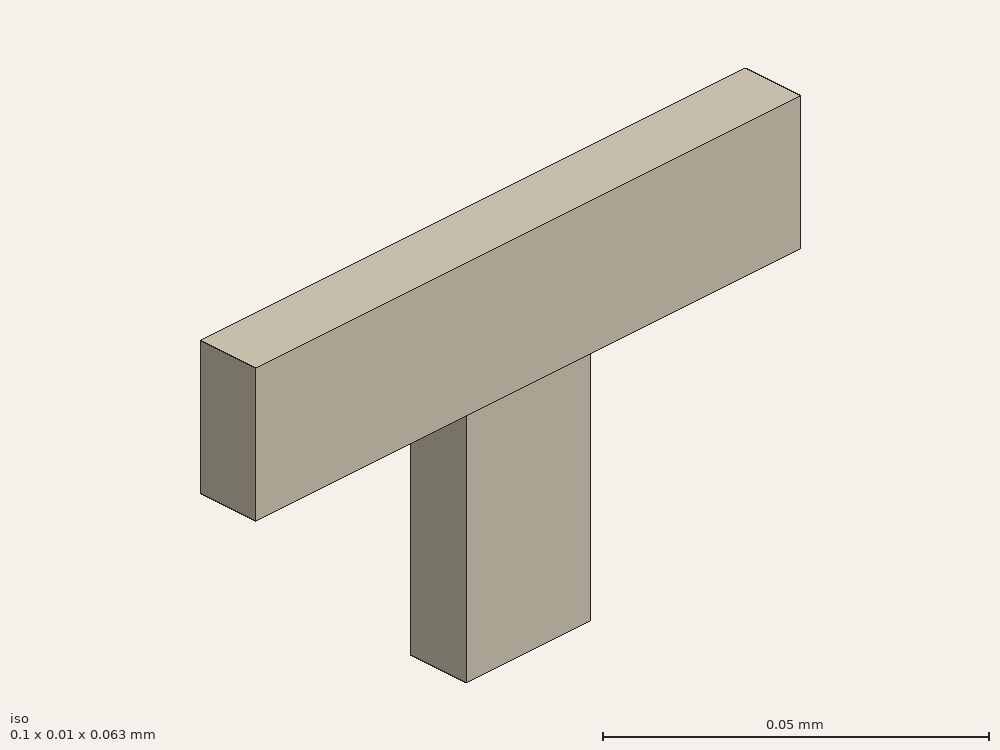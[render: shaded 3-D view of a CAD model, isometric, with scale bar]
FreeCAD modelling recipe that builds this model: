
FCSTD DOCUMENT  (FreeCAD 0.21R33694 (Git))
Label: tee
License: All rights reserved
LicenseURL: http://en.wikipedia.org/wiki/All_rights_reserved
objects: Part::Part2DObjectPython×8, App::FeaturePython×6, Part::Extrusion×2, Part::FeaturePython×2
note: 12 computed .brp shape members not serialized (recipe doc carries the construction recipe); baked Part::Feature solids carry a one-line shape summary decoded from their .brp

FEATURE [Part::Part2DObjectPython] Rectangle  # Draft 2D object (typed FeaturePython)
  Area = 232.258
  ChamferSize = 0
  Columns = 1
  FilletRadius = 0
  Height = 10.16
  Length = 22.86
  MakeFace = true
  Placement = pos=(-11.43,-5.08,0) rot=(0,0,1;0rad)
  Rows = 1
FEATURE [Part::Extrusion] Extrude
  Base = -> Rectangle
  Dir = (0,0,1)
  DirMode = 2
  FaceMakerClass = Part::FaceMakerBullseye
  LengthFwd = 40
  LengthRev = 0
  Solid = false
  Symmetric = false
FEATURE [Part::Part2DObjectPython] Rectangle001  label="_Pport1"  # Draft 2D object (typed FeaturePython)
  Area = 0.000232258
  ChamferSize = 0
  Columns = 1
  FilletRadius = 0
  Height = 0.01016
  Length = 0.02286
  MakeFace = true
  Placement = pos=(-0.01143,-0.00508,0) rot=(0,0,1;0rad)
  Rows = 1
FEATURE [Part::Part2DObjectPython] Line  label="_Pv1"  # Draft 2D object (typed FeaturePython)
  Area = 0
  ChamferSize = 0
  Closed = false
  End = (-1.8e-15,0.00508,0)
  FilletRadius = 0
  Length = 0.01016
  MakeFace = true
  Placement = pos=(0,-0.00508,0) rot=(0,0,1;0rad)
  Points = (2) [(0,0,0),(-1.77605e-15,0.01016,0)]
  Start = (0,-0.00508,0)
  Subdivisions = 0
FEATURE [App::FeaturePython] Text  label="_S1(PV){port1}"  # WARN: FeaturePython — macro-defined, semantics opaque (R4)
  Placement = pos=(0.0413747,-0.017509,0) rot=(0,0,1;0rad)
  Text = .
FEATURE [App::FeaturePython] Text001  label="_S2(PV){port2}"  # WARN: FeaturePython — macro-defined, semantics opaque (R4)
  Placement = pos=(0.0413747,-0.017509,0) rot=(0,0,1;0rad)
  Text = .
FEATURE [App::FeaturePython] Text002  label="_L1(1,voltage){v1}"  # WARN: FeaturePython — macro-defined, semantics opaque (R4)
  Placement = pos=(0.0413747,-0.017509,0) rot=(0,0,1;0rad)
  Text = .
FEATURE [App::FeaturePython] Text003  label="_L2(2,voltage){v2}"  # WARN: FeaturePython — macro-defined, semantics opaque (R4)
  Placement = pos=(0.0413747,-0.017509,0) rot=(0,0,1;0rad)
  Text = .
FEATURE [Part::Part2DObjectPython] Rectangle003  # Draft 2D object (typed FeaturePython)
  Area = 232.258
  ChamferSize = 0
  Columns = 1
  FilletRadius = 0
  Height = 10.16
  Length = 22.86
  MakeFace = true
  Placement = pos=(-11.43,-5.08,100) rot=(0,0,1;0rad)
  Rows = 1
FEATURE [Part::Extrusion] Extrude001
  Base = -> Rectangle003
  Dir = (0,0,1)
  DirMode = 2
  FaceMakerClass = Part::FaceMakerBullseye
  LengthFwd = 100
  LengthRev = 0
  Placement = pos=(150,0,51.43) rot=(0,-1,0;1.5708rad)
  Solid = false
  Symmetric = false
FEATURE [Part::FeaturePython] BooleanFragments  # WARN: FeaturePython — macro-defined, semantics opaque (R4)
  Mode = 0
  Objects = -> [Extrude,Extrude001]
  Tolerance = 0
FEATURE [Part::FeaturePython] Clone  label="scaled"  # Draft clone (typed FeaturePython)
  AttacherType = Attacher::AttachEngine3D
  Fuse = false
  Objects = -> [BooleanFragments]
  Scale = (0.001,0.001,0.001)
FEATURE [Part::Part2DObjectPython] Rectangle004  label="_Pport2"  # Draft 2D object (typed FeaturePython)
  Area = 0.000232258
  ChamferSize = 0
  Columns = 1
  FilletRadius = 0
  Height = 0.02286
  Length = 0.01016
  MakeFace = true
  Placement = pos=(0.05,-0.00508,0.04) rot=(0.57735,0.57735,0.57735;2.0944rad)
  Rows = 1
FEATURE [Part::Part2DObjectPython] Line002  label="_Pv2"  # Draft 2D object (typed FeaturePython)
  Area = 0
  ChamferSize = 0
  Closed = false
  End = (0.05,0.00508,0.05143)
  FilletRadius = 0
  Length = 0.01016
  MakeFace = true
  Placement = pos=(0.05,-0.00508,0.05143) rot=(0.57735,0.57735,0.57735;2.0944rad)
  Points = (2) [(0,0,0),(0.01016,7.10543e-15,0)]
  Start = (0.05,-0.00508,0.05143)
  Subdivisions = 0
FEATURE [Part::Part2DObjectPython] Rectangle005  label="_Pport3"  # Draft 2D object (typed FeaturePython)
  Area = 0.000232258
  ChamferSize = 0
  Columns = 1
  FilletRadius = 0
  Height = 0.02286
  Length = 0.01016
  MakeFace = true
  Placement = pos=(-0.05,0.00508,0.04) rot=(0.57735,-0.57735,-0.57735;2.0944rad)
  Rows = 1
FEATURE [Part::Part2DObjectPython] Line003  label="_Pv3"  # Draft 2D object (typed FeaturePython)
  Area = 0
  ChamferSize = 0
  Closed = false
  End = (-0.05,0.00508,0.05143)
  FilletRadius = 0
  Length = 0.01016
  MakeFace = true
  Placement = pos=(-0.05,-0.00508,0.05143) rot=(0.57735,-0.57735,-0.57735;2.0944rad)
  Points = (2) [(0,0,0),(-0.01016,7.10543e-15,0)]
  Start = (-0.05,-0.00508,0.05143)
  Subdivisions = 0
FEATURE [App::FeaturePython] Text004  label="_S3(PV){port3}"  # WARN: FeaturePython — macro-defined, semantics opaque (R4)
  Placement = pos=(0.0413747,-0.017509,0) rot=(0,0,1;0rad)
  Text = .
FEATURE [App::FeaturePython] Text005  label="_L3(3,voltage){v3}"  # WARN: FeaturePython — macro-defined, semantics opaque (R4)
  Placement = pos=(0.0413747,-0.017509,0) rot=(0,0,1;0rad)
  Text = .
